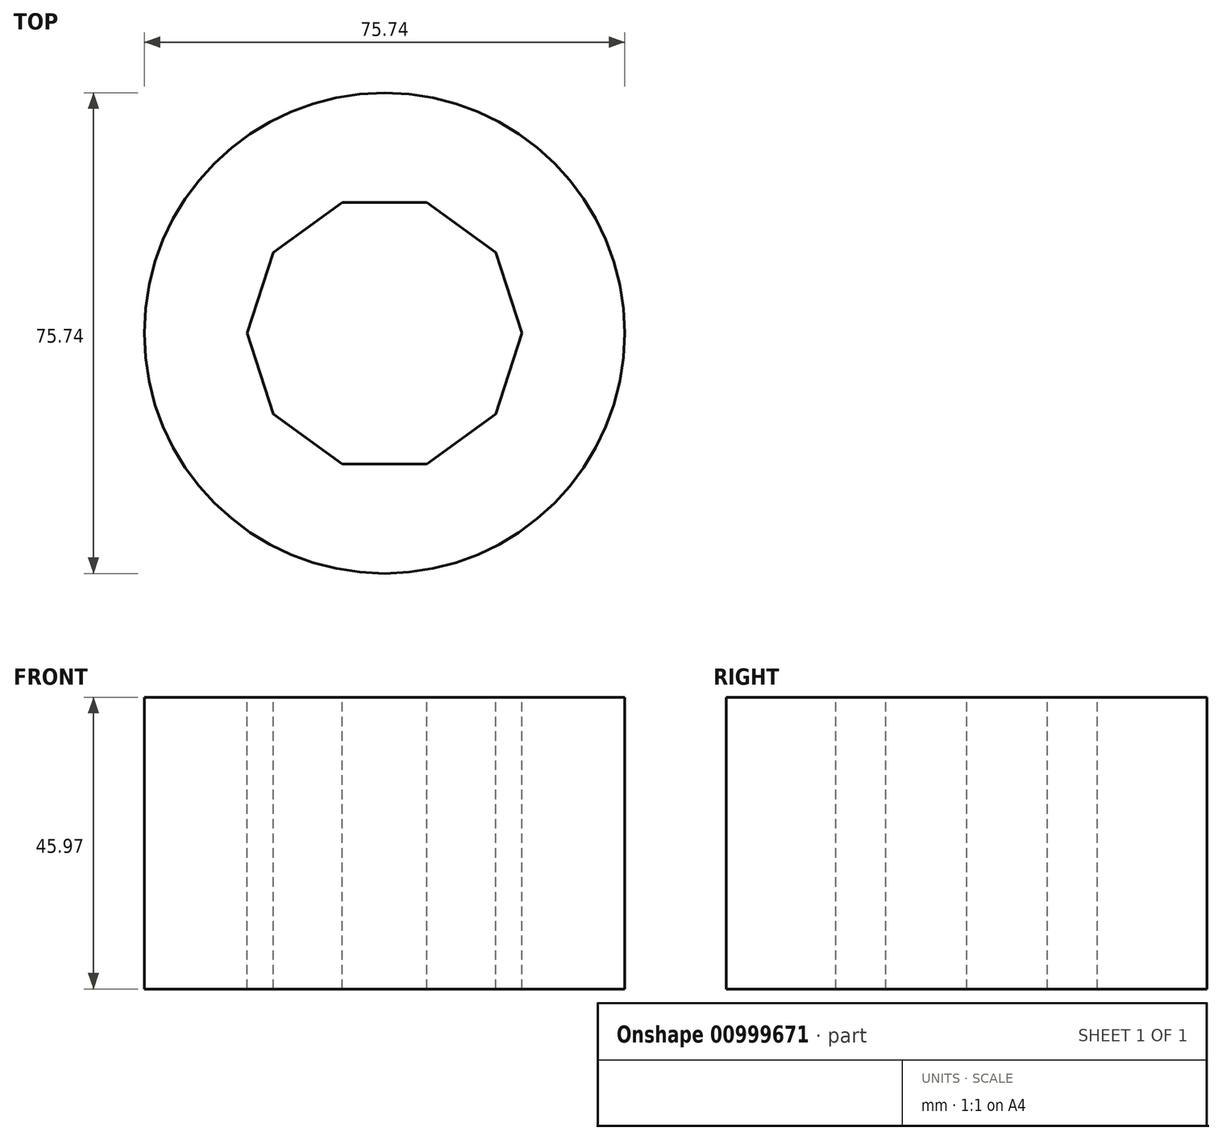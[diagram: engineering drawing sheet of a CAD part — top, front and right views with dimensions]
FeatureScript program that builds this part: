
annotation { "Feature Type Name" : "Feature", "Feature Type Description" : "" }
export const myFeature = defineFeature(function(context is Context, id is Id, definition is map)
    precondition{}
    {
        {
            var Q0;
            Q0=qCreatedBy(makeId("Top.planeOp"),FACE);
            var sketch = newSketch(context, id + "F0", { "sketchPlane" : qUnion([Q0])});
            skCircle(sketch, "E0", {"center": v(0, 0) * mm, "radius": 37.87 * mm});
            skSolve(sketch);
        }
        {
            var Q0;
            Q0=makeQuery(id+"F0.imprint","IMPRINT",FACE,{"disambiguationData":[TD([[makeQuery(id+"F0.imprint","IMPRINT",EDGE,{"derivedFrom":sQuery(id+"F0.wireOp",EDGE,"E0")}),1.0]])]});
            extrude(context, id + "F1", {"entities" : qUnion([Q0]), "depth" : 45.97 * mm, "offsetDistance" : 25.4 * mm});
        }
        {
            var Q0;
            Q0=makeQuery(id+"F1.opExtrude","CAP_FACE",FACE,{"disambiguationData":[OSD([sQuery(id+"F0.wireOp",EDGE,"E0")])],"isStart":false});
            var sketch = newSketch(context, id + "F2", { "sketchPlane" : qUnion([Q0])});
            skCircle(sketch, "E1.cCircle", {"center": v(0, 0) * mm, "radius": 20.6 * mm, "construction": true});
            skLineSegment(sketch, "E1.0", {"start": v(-6.7, 20.6) * mm, "end": v(6.7, 20.6) * mm});
            skLineSegment(sketch, "E1.1", {"start": v(6.7, 20.6) * mm, "end": v(17.52, 12.73) * mm});
            skLineSegment(sketch, "E1.2", {"start": v(17.52, 12.73) * mm, "end": v(21.65, 0) * mm});
            skLineSegment(sketch, "E1.3", {"start": v(21.65, 0) * mm, "end": v(17.52, -12.73) * mm});
            skLineSegment(sketch, "E1.4", {"start": v(17.52, -12.73) * mm, "end": v(6.7, -20.6) * mm});
            skLineSegment(sketch, "E1.5", {"start": v(6.7, -20.6) * mm, "end": v(-6.7, -20.6) * mm});
            skLineSegment(sketch, "E1.6", {"start": v(-6.7, -20.6) * mm, "end": v(-17.52, -12.73) * mm});
            skLineSegment(sketch, "E1.7", {"start": v(-17.52, -12.73) * mm, "end": v(-21.65, 0) * mm});
            skLineSegment(sketch, "E1.8", {"start": v(-21.65, 0) * mm, "end": v(-17.52, 12.73) * mm});
            skLineSegment(sketch, "E1.9", {"start": v(-17.52, 12.73) * mm, "end": v(-6.7, 20.6) * mm});
            skPoint(sketch, "E1.0.midPoint", {"position": v(0, 20.6) * mm});
            skSolve(sketch);
        }
        {
            var Q0;
            Q0=makeQuery(id+"F2.imprint","IMPRINT",FACE,{"disambiguationData":[TD([[makeQuery(id+"F2.imprint","IMPRINT",EDGE,{"derivedFrom":sQuery(id+"F2.wireOp",EDGE,"E1.0")}),-1.0]])]});
            extrude(context, id + "F3", {"entities" : qUnion([Q0]), "operationType" : NewBodyOperationType.REMOVE, "oppositeDirection" : true, "depth" : 25.4 * mm, "offsetDistance" : 25.4 * mm});
        }
        {
            var Q0;
            Q0=makeQuery(id+"F3.boolean.opBoolean","COPY",FACE,{"derivedFrom":makeQuery(id+"F3.opExtrude","CAP_FACE",FACE,{"disambiguationData":[OSD([sQuery(id+"F2.wireOp",EDGE,"E1.0"),sQuery(id+"F2.wireOp",EDGE,"E1.1"),sQuery(id+"F2.wireOp",EDGE,"E1.2"),sQuery(id+"F2.wireOp",EDGE,"E1.3"),sQuery(id+"F2.wireOp",EDGE,"E1.4"),sQuery(id+"F2.wireOp",EDGE,"E1.5"),sQuery(id+"F2.wireOp",EDGE,"E1.6"),sQuery(id+"F2.wireOp",EDGE,"E1.7"),sQuery(id+"F2.wireOp",EDGE,"E1.8"),sQuery(id+"F2.wireOp",EDGE,"E1.9")])],"isStart":false})});
            extrude(context, id + "F4", {"entities" : qUnion([Q0]), "operationType" : NewBodyOperationType.REMOVE, "endBound" : BoundingType.THROUGH_ALL, "oppositeDirection" : true, "depth" : 25.4 * mm, "offsetDistance" : 25.4 * mm});
        }
    });
